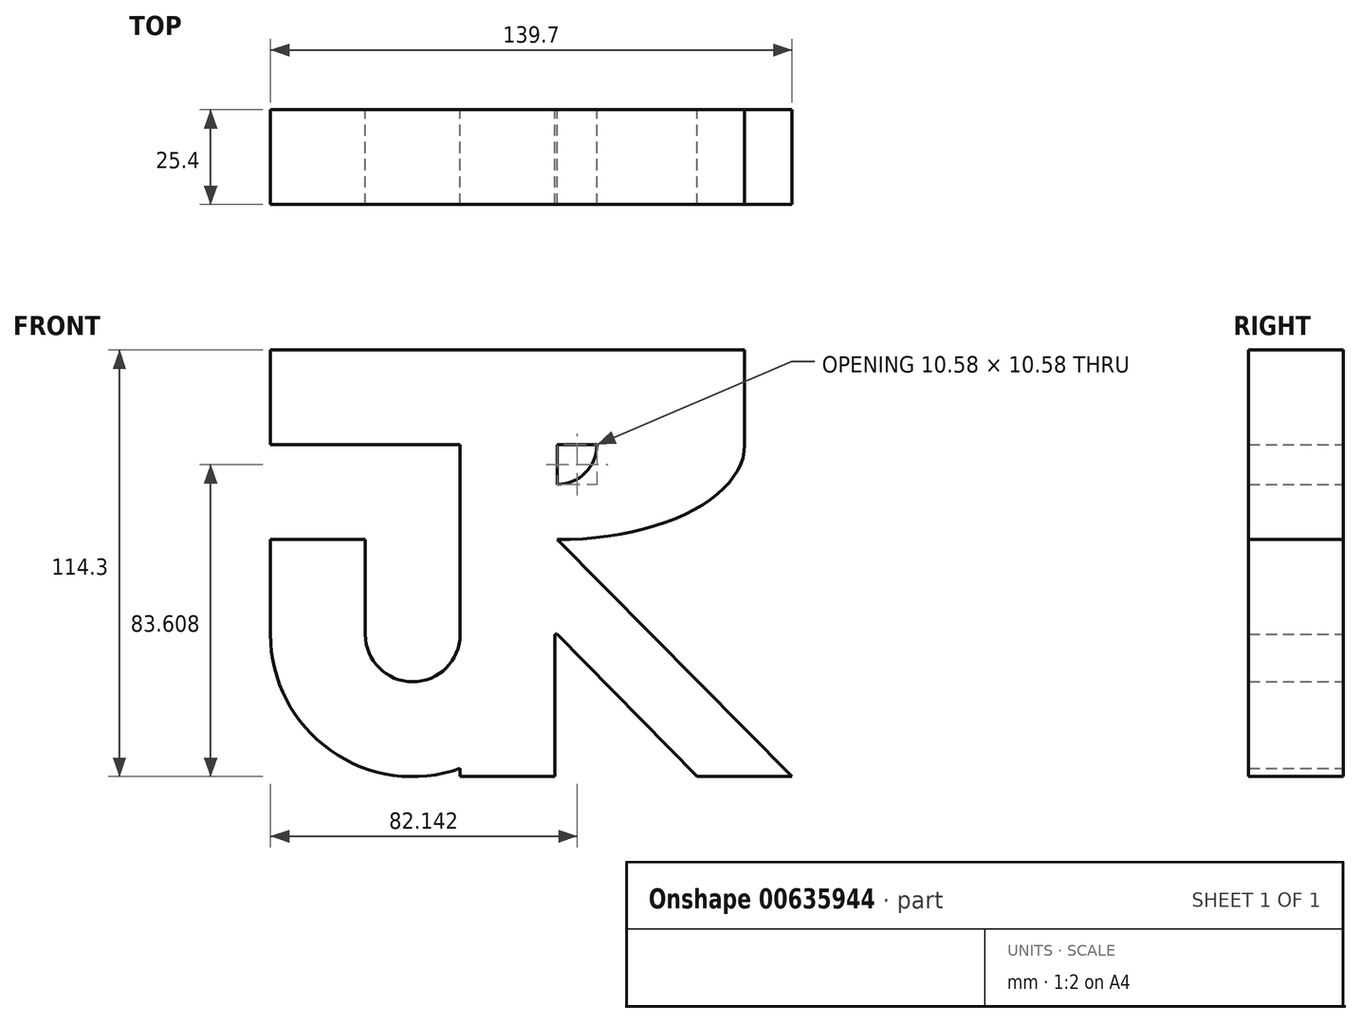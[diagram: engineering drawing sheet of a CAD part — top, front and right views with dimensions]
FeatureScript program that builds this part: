
annotation { "Feature Type Name" : "Feature", "Feature Type Description" : "" }
export const myFeature = defineFeature(function(context is Context, id is Id, definition is map)
    precondition{}
    {
        {
            var Q0;
            Q0=qCreatedBy(makeId("Front.planeOp"),FACE);
            var sketch = newSketch(context, id + "F0", { "sketchPlane" : qUnion([Q0]), "disableImprinting" : false});
            skLineSegment(sketch, "E0.bottom", {"start": v(0, 25.4) * mm, "end": v(0, 25.4) * mm});
            skLineSegment(sketch, "E0.top", {"start": v(0, -25.4) * mm, "end": v(0, -25.4) * mm});
            skLineSegment(sketch, "E0.left", {"start": v(0, 25.4) * mm, "end": v(0, 0) * mm});
            skLineSegment(sketch, "E0.right", {"start": v(0, 25.4) * mm, "end": v(0, 0) * mm});
            skPoint(sketch, "E0.middle", {"position": v(0, 0) * mm});
            skLineSegment(sketch, "E1.bottom", {"start": v(0, 25.4) * mm, "end": v(-26.05, 25.4) * mm});
            skLineSegment(sketch, "E1.top", {"start": v(0, -25.4) * mm, "end": v(-26.05, -25.4) * mm});
            skLineSegment(sketch, "E1.right", {"start": v(-26.05, 25.4) * mm, "end": v(-26.05, -25.4) * mm});
            skLineSegment(sketch, "E2.bottom", {"start": v(-0.65, -25.4) * mm, "end": v(0, -25.4) * mm});
            skLineSegment(sketch, "E2.top", {"start": v(-0.65, 25.4) * mm, "end": v(0, 25.4) * mm});
            skLineSegment(sketch, "E2.right", {"start": v(-0.65, -25.4) * mm, "end": v(-0.65, 25.4) * mm});
            skLineSegment(sketch, "E3.bottom", {"start": v(-26.05, 25.4) * mm, "end": v(-0.65, 25.4) * mm});
            skLineSegment(sketch, "E3.top", {"start": v(-26.05, 50.8) * mm, "end": v(-0.65, 50.8) * mm});
            skLineSegment(sketch, "E3.left", {"start": v(-26.05, 25.4) * mm, "end": v(-26.05, 50.8) * mm});
            skLineSegment(sketch, "E3.right", {"start": v(-0.65, 25.4) * mm, "end": v(-0.65, 50.8) * mm});
            skLineSegment(sketch, "E4.bottom", {"start": v(-26.05, 25.4) * mm, "end": v(-76.85, 25.4) * mm});
            skLineSegment(sketch, "E4.top", {"start": v(-26.05, 50.8) * mm, "end": v(-76.85, 50.8) * mm});
            skLineSegment(sketch, "E4.right", {"start": v(-76.85, 25.4) * mm, "end": v(-76.85, 50.8) * mm});
            skLineSegment(sketch, "E5.top", {"start": v(-76.85, 0) * mm, "end": v(-51.45, 0) * mm});
            skLineSegment(sketch, "E5.left", {"start": v(-76.85, -25.4) * mm, "end": v(-76.85, 0) * mm});
            skLineSegment(sketch, "E5.right", {"start": v(-51.45, -25.4) * mm, "end": v(-51.45, 0) * mm});
            skArc(sketch, "E6", {"start": v(-76.85, -25.4) * mm, "mid": v(-38.75, -63.5) * mm, "end": v(-0.65, -25.4) * mm});
            skArc(sketch, "E7", {"start": v(-51.45, -25.4) * mm, "mid": v(-38.75, -38.1) * mm, "end": v(-26.05, -25.4) * mm});
            skLineSegment(sketch, "E8.bottom", {"start": v(-0.65, 50.8) * mm, "end": v(50.15, 50.8) * mm});
            skLineSegment(sketch, "E8.top", {"start": v(-0.65, 25.4) * mm, "end": v(50.15, 25.4) * mm});
            skLineSegment(sketch, "E8.left", {"start": v(-0.65, 50.8) * mm, "end": v(-0.65, 25.4) * mm});
            skLineSegment(sketch, "E8.right", {"start": v(50.15, 50.8) * mm, "end": v(50.15, 25.4) * mm});
            skPoint(sketch, "E9.oppositeSnap0", {"position": v(-38.75, -63.5) * mm});
            skLineSegment(sketch, "E9.top", {"start": v(-26.05, -63.5) * mm, "end": v(-0.65, -63.5) * mm});
            skLineSegment(sketch, "E9.left", {"start": v(-26.05, -25.4) * mm, "end": v(-26.05, -63.5) * mm});
            skLineSegment(sketch, "E9.right", {"start": v(-0.65, -25.4) * mm, "end": v(-0.65, -63.5) * mm});
            skEllipticalArc(sketch, "E10", {});
            skLineSegment(sketch, "E11", {"start": v(50.15, -63.5) * mm, "end": v(37.45, -63.5) * mm});
            skLineSegment(sketch, "E12", {"start": v(50.15, -63.5) * mm, "end": v(62.85, -63.5) * mm});
            skLineSegment(sketch, "E13", {"start": v(37.45, -63.5) * mm, "end": v(0, -25.4) * mm});
            skLineSegment(sketch, "E14", {"start": v(62.85, -63.5) * mm, "end": v(0, 0) * mm});
            skPoint(sketch, "E15.MirrorCS.end.orphan", {"position": v(-76.85, 0) * mm});
            skPoint(sketch, "E15.MirrorCS.start.orphan", {"position": v(-76.85, 25.4) * mm});
            skArc(sketch, "E16", {"start": v(10.58, 25.4) * mm, "mid": v(7.48, 17.92) * mm, "end": v(0, 14.82) * mm});
            const initialGuessF0  = {"E10": [0, 0.0254, 0, -1, 0.0254, 0.050148289322853104, 6.270189270193363, 3.154588690576017]};
            skSetInitialGuess(sketch, initialGuessF0);
            skSolve(sketch);
        }
        {
            var Q0;
            Q0 = qSketchRegion(id + "F0", true);
            extrude(context, id + "F1", {"entities" : qUnion([Q0]), "depth" : 25.4 * mm, "offsetDistance" : 25.4 * mm});
        }
    });
